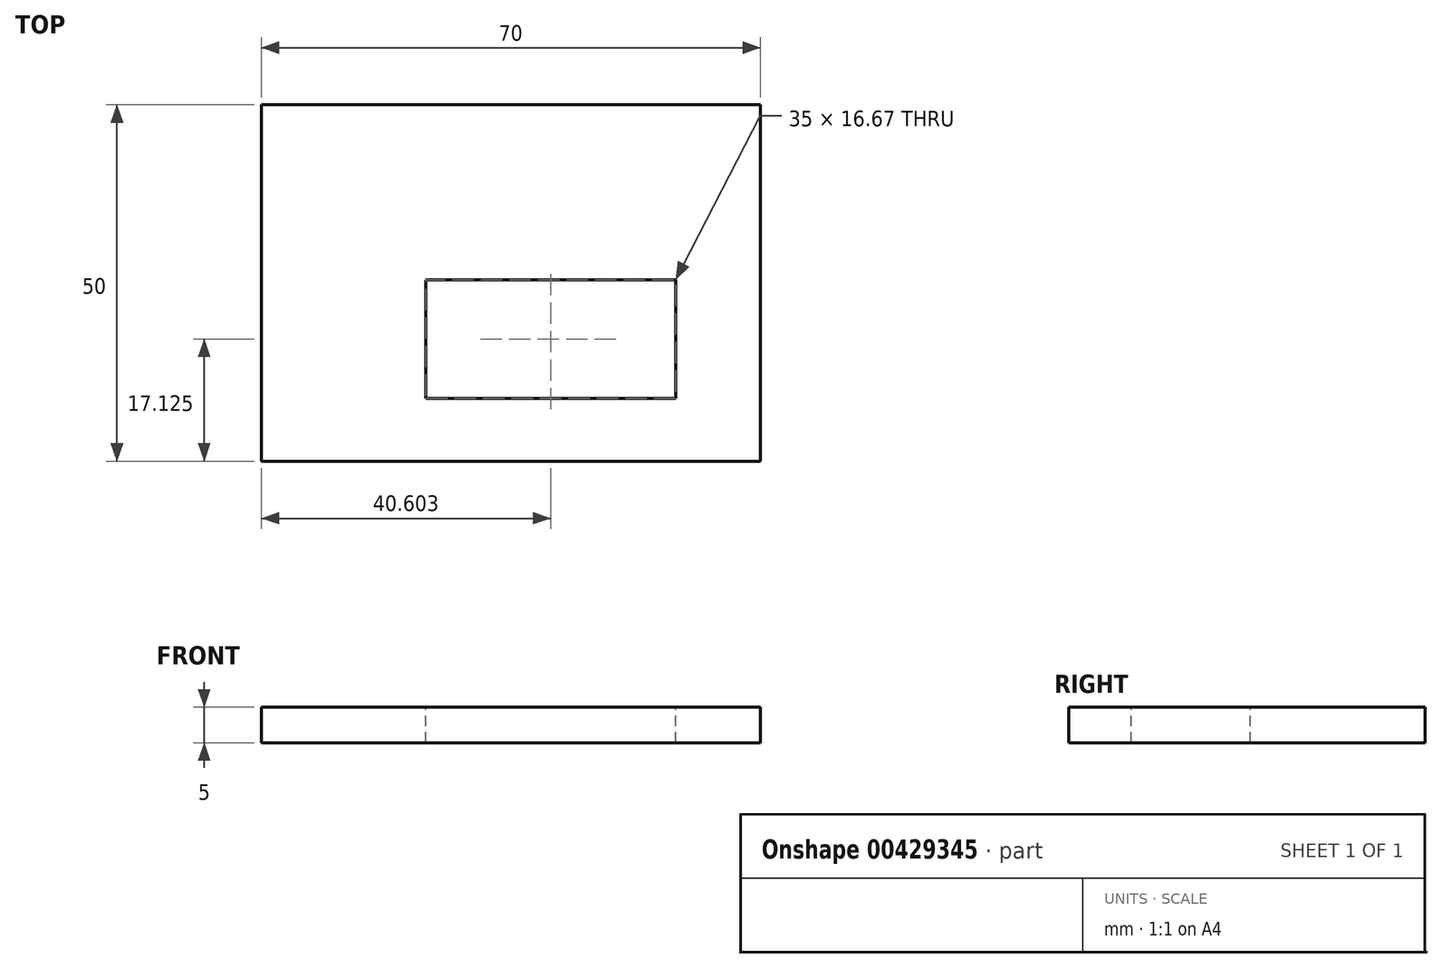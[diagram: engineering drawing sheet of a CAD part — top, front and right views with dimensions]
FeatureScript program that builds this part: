
annotation { "Feature Type Name" : "Feature", "Feature Type Description" : "" }
export const myFeature = defineFeature(function(context is Context, id is Id, definition is map)
    precondition{}
    {
        {
            assignVariable(context, id + "F0", {"name" : "thickness", "anyValue" : 5});
        }
        {
            var Q0;
            Q0=qCreatedBy(makeId("Top.planeOp"),FACE);
            var sketch = newSketch(context, id + "F1", { "sketchPlane" : qUnion([Q0])});
            skLineSegment(sketch, "E0.bottom", {"start": v(-28.47, 20.09) * mm, "end": v(41.53, 20.09) * mm});
            skLineSegment(sketch, "E0.top", {"start": v(-28.47, -29.91) * mm, "end": v(41.53, -29.91) * mm});
            skLineSegment(sketch, "E0.left", {"start": v(-28.47, 20.09) * mm, "end": v(-28.47, -29.91) * mm});
            skLineSegment(sketch, "E0.right", {"start": v(41.53, 20.09) * mm, "end": v(41.53, -29.91) * mm});
            skSolve(sketch);
        }
        {
            var Q0;
            Q0=makeQuery(id+"F1.imprint","IMPRINT",FACE,{"disambiguationData":[TD([[makeQuery(id+"F1.imprint","IMPRINT",EDGE,{"derivedFrom":sQuery(id+"F1.wireOp",EDGE,"E0.bottom")}),-1.0]])]});
            extrude(context, id + "F2", {"entities" : qUnion([Q0]), "depth" : (getVariable(context, 'thickness')) * mm});
        }
        {
            var Q0;
            Q0=makeQuery(id+"F2.opExtrude","CAP_FACE",FACE,{"disambiguationData":[OSD([sQuery(id+"F1.wireOp",EDGE,"E0.bottom"),sQuery(id+"F1.wireOp",EDGE,"E0.top"),sQuery(id+"F1.wireOp",EDGE,"E0.left"),sQuery(id+"F1.wireOp",EDGE,"E0.right")])],"isStart":false});
            var sketch = newSketch(context, id + "F3", { "sketchPlane" : qUnion([Q0])});
            skLineSegment(sketch, "E1.bottom", {"start": v(-5.37, -4.45) * mm, "end": v(29.63, -4.45) * mm});
            skLineSegment(sketch, "E1.top", {"start": v(-5.37, -21.12) * mm, "end": v(29.63, -21.12) * mm});
            skLineSegment(sketch, "E1.left", {"start": v(-5.37, -4.45) * mm, "end": v(-5.37, -21.12) * mm});
            skLineSegment(sketch, "E1.right", {"start": v(29.63, -4.45) * mm, "end": v(29.63, -21.12) * mm});
            skSolve(sketch);
        }
        {
            var Q0;
            Q0=makeQuery(id+"F3.imprint","IMPRINT",FACE,{"disambiguationData":[TD([[makeQuery(id+"F3.imprint","IMPRINT",EDGE,{"derivedFrom":sQuery(id+"F3.wireOp",EDGE,"E1.bottom")}),-1.0]])]});
            extrude(context, id + "F4", {"entities" : qUnion([Q0]), "operationType" : NewBodyOperationType.REMOVE, "oppositeDirection" : true, "depth" : 25 * mm});
        }
    });
